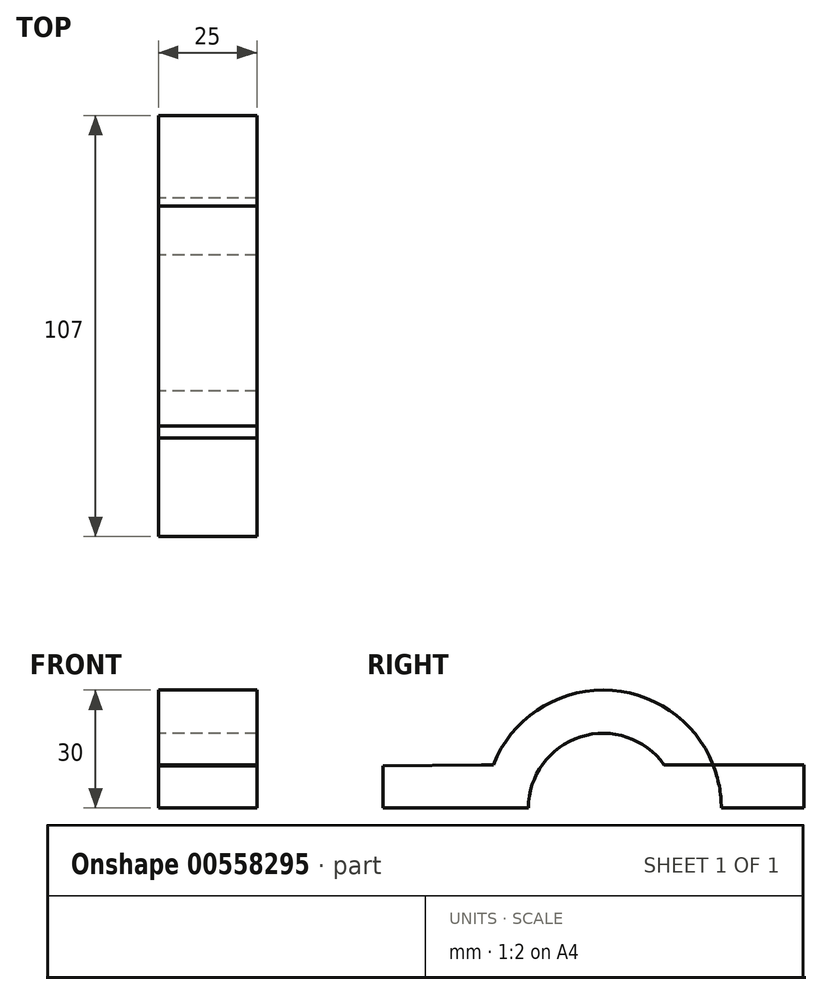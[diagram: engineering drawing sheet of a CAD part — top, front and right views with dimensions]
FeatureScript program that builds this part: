
annotation { "Feature Type Name" : "Feature", "Feature Type Description" : "" }
export const myFeature = defineFeature(function(context is Context, id is Id, definition is map)
    precondition{}
    {
        {
            var Q0;
            Q0=qCreatedBy(makeId("Right.planeOp"),FACE);
            var sketch = newSketch(context, id + "F0", { "sketchPlane" : qUnion([Q0])});
            skCircle(sketch, "E0", {"center": v(0, 0) * mm, "radius": 19 * mm});
            skCircle(sketch, "E1", {"center": v(0, 0) * mm, "radius": 30 * mm});
            skLineSegment(sketch, "E2.bottom", {"start": v(-56, 0) * mm, "end": v(25.94, 0) * mm});
            skLineSegment(sketch, "E2.top", {"start": v(-30.94, 11) * mm, "end": v(51, 11) * mm});
            skLineSegment(sketch, "E2.left", {"start": v(-30.94, 0) * mm, "end": v(-30.94, 11) * mm});
            skLineSegment(sketch, "E2.right", {"start": v(51, 0) * mm, "end": v(51, 11) * mm});
            skLineSegment(sketch, "E3.bottom", {"start": v(51, 11) * mm, "end": v(40, 11) * mm});
            skLineSegment(sketch, "E3.top", {"start": v(51, 41) * mm, "end": v(40, 41) * mm});
            skLineSegment(sketch, "E3.left", {"start": v(51, 11) * mm, "end": v(51, 41) * mm});
            skLineSegment(sketch, "E3.right", {"start": v(40, 11) * mm, "end": v(40, 41) * mm});
            skLineSegment(sketch, "E4", {"start": v(25.94, 0) * mm, "end": v(51, 0) * mm});
            skLineSegment(sketch, "E5", {"start": v(-56, 0) * mm, "end": v(-56, 10.71) * mm});
            skLineSegment(sketch, "E6", {"start": v(-56, 10.71) * mm, "end": v(-30.94, 11) * mm});
            skSolve(sketch);
        }
        {
            var Q0;
            {var subQ0=sQuery(id+"F0.wireOp",EDGE,"E2.top");var subQ1=sQuery(id+"F0.wireOp",EDGE,"E0");var subQ2=makeQuery(id+"F0.imprint","INTERSECT",VERTEX,{"disambiguationData":[OD(0.0)],"derivedFrom":[subQ1,subQ0]});Q0=makeQuery(id+"F0.imprint","IMPRINT",FACE,{"disambiguationData":[TD([[makeQuery(id+"F0.imprint","IMPRINT",EDGE,{"disambiguationData":[TD([[subQ2,-1.0]])],"derivedFrom":subQ1}),-1.0]])]});}
            var Q1;
            {var subQ0=sQuery(id+"F0.wireOp",EDGE,"E2.top");var subQ1=sQuery(id+"F0.wireOp",EDGE,"E0");var subQ2=makeQuery(id+"F0.imprint","INTERSECT",VERTEX,{"disambiguationData":[OD(1.0)],"derivedFrom":[subQ1,subQ0]});Q1=makeQuery(id+"F0.imprint","IMPRINT",FACE,{"disambiguationData":[TD([[makeQuery(id+"F0.imprint","IMPRINT",EDGE,{"disambiguationData":[TD([[subQ2,-1.0]])],"derivedFrom":subQ1}),-1.0]])]});}
            var Q2;
            {var subQ3=sQuery(id+"F0.wireOp",EDGE,"E0");var subQ5=sQuery(id+"F0.wireOp",EDGE,"E2.top");var subQ6=makeQuery(id+"F0.imprint","INTERSECT",VERTEX,{"disambiguationData":[OD(0.0)],"derivedFrom":[subQ3,subQ5]});Q2=makeQuery(id+"F0.imprint","IMPRINT",FACE,{"disambiguationData":[TD([[makeQuery(id+"F0.imprint","IMPRINT",EDGE,{"disambiguationData":[TD([[subQ6,1.0]])],"derivedFrom":subQ3}),-1.0]])]});}
            var Q3;
            {var subQ0=sQuery(id+"F0.wireOp",EDGE,"E2.right");Q3=makeQuery(id+"F0.imprint","IMPRINT",FACE,{"disambiguationData":[TD([[makeQuery(id+"F0.imprint","IMPRINT",EDGE,{"derivedFrom":subQ0}),1.0]])]});}
            var Q4;
            {var subQ5=sQuery(id+"F0.wireOp",EDGE,"E2.left");Q4=makeQuery(id+"F0.imprint","IMPRINT",FACE,{"disambiguationData":[TD([[makeQuery(id+"F0.imprint","IMPRINT",EDGE,{"derivedFrom":subQ5}),-1.0]])]});}
            var Q5;
            Q5=makeQuery(id+"F0.imprint","IMPRINT",FACE,{"disambiguationData":[TD([[makeQuery(id+"F0.imprint","IMPRINT",EDGE,{"derivedFrom":sQuery(id+"F0.wireOp",EDGE,"E3.bottom")}),-1.0]])]});
            var Q6;
            {var subQ2=sQuery(id+"F0.wireOp",EDGE,"E2.left");Q6=makeQuery(id+"F0.imprint","IMPRINT",FACE,{"disambiguationData":[TD([[makeQuery(id+"F0.imprint","IMPRINT",EDGE,{"derivedFrom":subQ2}),1.0]])]});}
            extrude(context, id + "F1", {"entities" : qUnion([Q0, Q1, Q2, Q3, Q4, Q5, Q6]), "endBound" : BoundingType.SYMMETRIC, "depth" : 25 * mm, "offsetDistance" : 25 * mm});
        }
        {
            var Q0;
            Q0=makeQuery(id+"F1.opExtrude","SWEPT_FACE",FACE,{"disambiguationData":[OSD([sQuery(id+"F0.wireOp",EDGE,"E2.right"),sQuery(id+"F0.wireOp",EDGE,"E3.left")])]});
            var sketch = newSketch(context, id + "F2", { "sketchPlane" : qUnion([Q0])});
            skLineSegment(sketch, "E7", {"start": v(0, 41.01) * mm, "end": v(0, 0) * mm, "construction": true});
            skCircle(sketch, "E8", {"center": v(0, 25) * mm, "radius": 6.5 * mm});
            skLineSegment(sketch, "E9", {"start": v(-6.5, 25) * mm, "end": v(-6.5, 41) * mm});
            skLineSegment(sketch, "E10", {"start": v(6.5, 25) * mm, "end": v(6.5, 41) * mm});
            skLineSegment(sketch, "E11", {"start": v(-6.5, 41) * mm, "end": v(6.5, 41) * mm});
            skSolve(sketch);
        }
        {
            var Q0;
            {var subQ0=sQuery(id+"F2.wireOp",EDGE,"E9");Q0=makeQuery(id+"F2.imprint","IMPRINT",FACE,{"disambiguationData":[TD([[makeQuery(id+"F2.imprint","IMPRINT",EDGE,{"derivedFrom":subQ0}),-1.0]])]});}
            var Q1;
            {var subQ0=sQuery(id+"F2.wireOp",EDGE,"E8");var subQ1=makeQuery(id+"F2.imprint","INTERSECT",VERTEX,{"derivedFrom":[subQ0,sQuery(id+"F2.wireOp",EDGE,"E9")]});Q1=makeQuery(id+"F2.imprint","IMPRINT",FACE,{"disambiguationData":[TD([[makeQuery(id+"F2.imprint","IMPRINT",EDGE,{"disambiguationData":[TD([[subQ1,1.0]])],"derivedFrom":subQ0}),1.0]])]});}
            extrude(context, id + "F3", {"entities" : qUnion([Q0, Q1]), "operationType" : NewBodyOperationType.REMOVE, "endBound" : BoundingType.SYMMETRIC, "oppositeDirection" : true, "depth" : 25 * mm, "offsetDistance" : 25 * mm});
        }
    });
